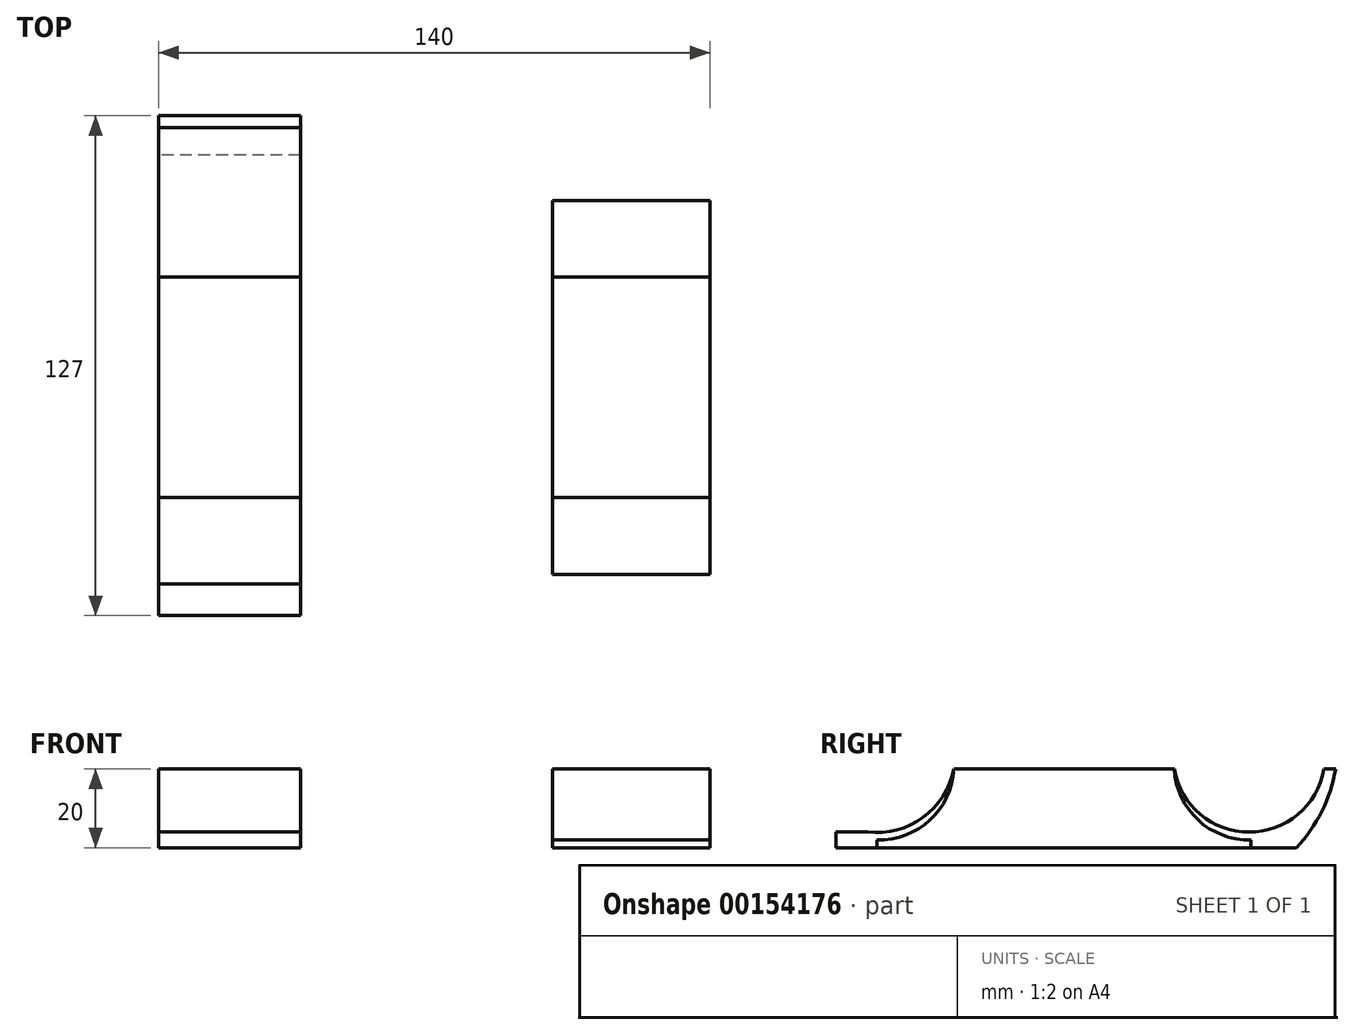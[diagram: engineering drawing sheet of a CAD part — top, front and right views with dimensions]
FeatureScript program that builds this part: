
annotation { "Feature Type Name" : "Feature", "Feature Type Description" : "" }
export const myFeature = defineFeature(function(context is Context, id is Id, definition is map)
    precondition{}
    {
        {
            var Q0;
            Q0=qCreatedBy(makeId("Right.planeOp"),FACE);
            var sketch = newSketch(context, id + "F0", { "sketchPlane" : qUnion([Q0])});
            skPoint(sketch, "E0", {"position": v(28, 0) * mm});
            skLineSegment(sketch, "E1", {"start": v(28, 0) * mm, "end": v(-28, 0) * mm});
            skPoint(sketch, "E2", {"position": v(0, -20) * mm});
            skPoint(sketch, "E3", {"position": v(47.5, -20) * mm});
            skLineSegment(sketch, "E4", {"start": v(47.5, -20) * mm, "end": v(-47.5, -20) * mm});
            skLineSegment(sketch, "E5", {"start": v(-47.5, -20) * mm, "end": v(-47.5, -18) * mm});
            skLineSegment(sketch, "E6", {"start": v(47.5, -20) * mm, "end": v(47.5, -18) * mm});
            skArc(sketch, "E7", {"start": v(-47.5, -18) * mm, "mid": v(-34.09, -12.97) * mm, "end": v(-28, 0) * mm});
            skArc(sketch, "E8", {"start": v(28, 0) * mm, "mid": v(34.09, -12.97) * mm, "end": v(47.5, -18) * mm});
            skSolve(sketch);
        }
        {
            var Q0;
            Q0=qSketchRegion(id+"F0",true);
            extrude(context, id + "F1", {"entities" : qUnion([Q0]), "depth" : 40 * mm, "offsetDistance" : 25 * mm});
        }
        {
            var Q0;
            Q0=qCreatedBy(makeId("Right.planeOp"),FACE);
            cPlane(context, id + "F2", {"entities" : qUnion([Q0]), "cplaneType" : CPlaneType.OFFSET, "offset" : 100 * mm, "oppositeDirection" : true, "width" : 150 * mm, "height" : 150 * mm});
        }
        {
            var Q0;
            Q0=qCreatedBy(id+"F2.planeOp",FACE);
            var sketch = newSketch(context, id + "F3", { "sketchPlane" : qUnion([Q0])});
            skPoint(sketch, "E9", {"position": v(-28, 0) * mm});
            skLineSegment(sketch, "E10", {"start": v(-28, 0) * mm, "end": v(28, 0) * mm});
            skPoint(sketch, "E11", {"position": v(47, 0) * mm});
            skPoint(sketch, "E12", {"position": v(0, -20) * mm});
            skPoint(sketch, "E13", {"position": v(-28, -20) * mm});
            skPoint(sketch, "E14", {"position": v(-58, -20) * mm});
            skLineSegment(sketch, "E15", {"start": v(-58, -20) * mm, "end": v(-58, -16) * mm});
            skLineSegment(sketch, "E16", {"start": v(-58, -16) * mm, "end": v(72, -16) * mm, "construction": true});
            skPoint(sketch, "E17", {"position": v(-50, -16) * mm});
            skArc(sketch, "E18", {"start": v(-50, -16) * mm, "mid": v(-35.86, -12.32) * mm, "end": v(-28, 0) * mm});
            skLineSegment(sketch, "E19", {"start": v(-50, -16) * mm, "end": v(-58, -16) * mm});
            skLineSegment(sketch, "E20", {"start": v(-58, -20) * mm, "end": v(0, -20) * mm});
            skPoint(sketch, "E21", {"position": v(66, 0) * mm});
            skPoint(sketch, "E22", {"position": v(47, -16) * mm});
            skArc(sketch, "E23", {"start": v(28, 0) * mm, "mid": v(47, -16) * mm, "end": v(66, 0) * mm});
            skPoint(sketch, "E24", {"position": v(47, -20) * mm});
            skLineSegment(sketch, "E25", {"start": v(0, -20) * mm, "end": v(47, -20) * mm});
            skLineSegment(sketch, "E26", {"start": v(47, -20) * mm, "end": v(59, -20) * mm});
            skLineSegment(sketch, "E27", {"start": v(66, 0) * mm, "end": v(69, 0) * mm});
            skArc(sketch, "E28", {"start": v(59, -20) * mm, "mid": v(65.5, -10.75) * mm, "end": v(69, 0) * mm});
            skSolve(sketch);
        }
        {
            var Q0;
            Q0=qSketchRegion(id+"F3",true);
            extrude(context, id + "F4", {"entities" : qUnion([Q0]), "depth" : 36 * mm, "offsetDistance" : 25 * mm});
        }
    });
